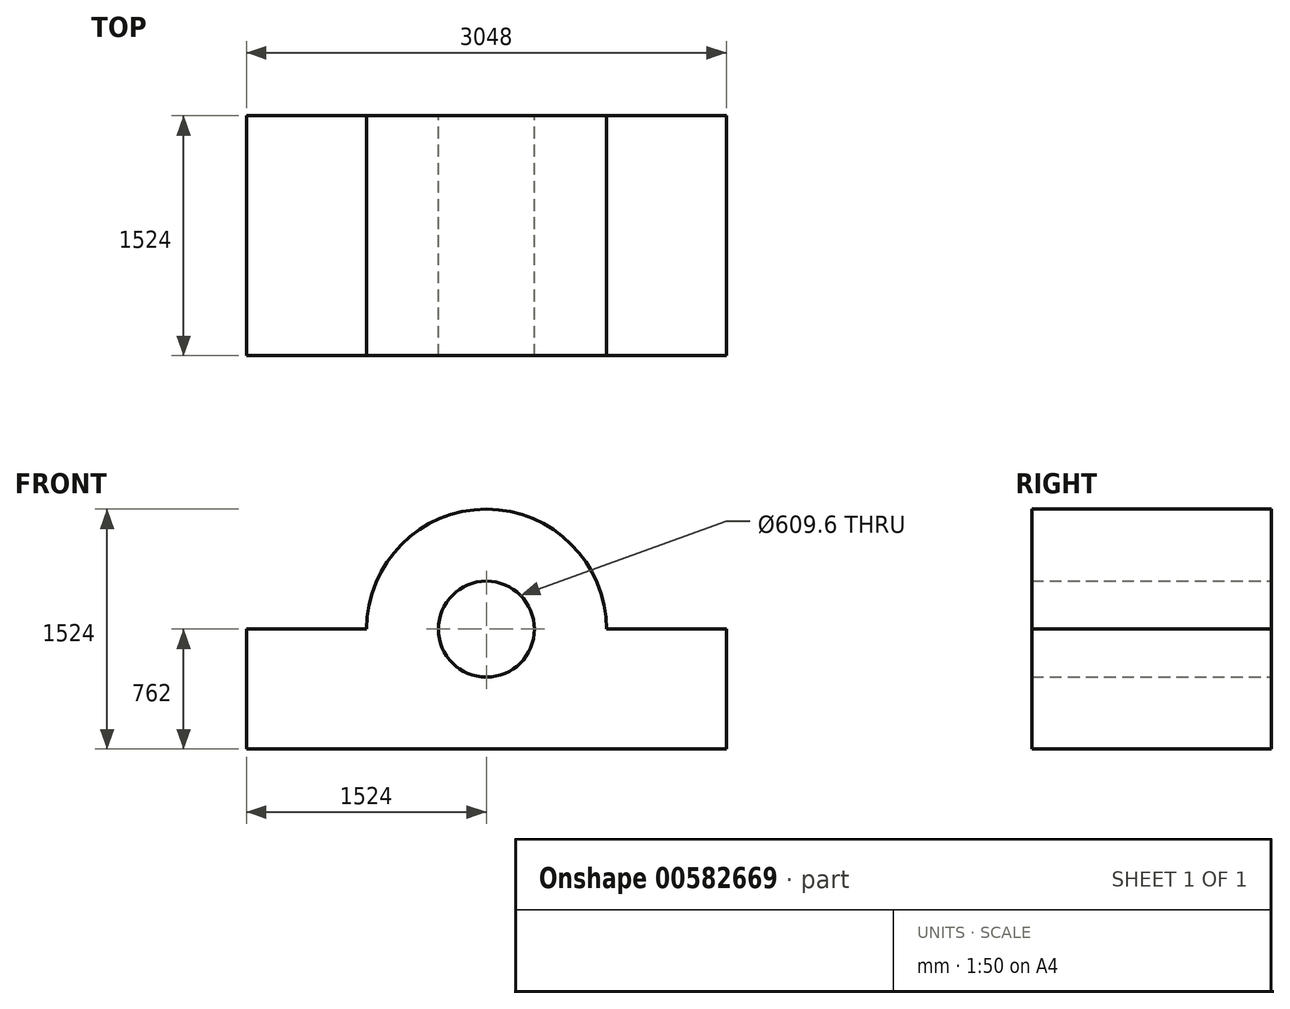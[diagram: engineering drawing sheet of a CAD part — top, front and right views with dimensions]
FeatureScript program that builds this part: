
annotation { "Feature Type Name" : "Feature", "Feature Type Description" : "" }
export const myFeature = defineFeature(function(context is Context, id is Id, definition is map)
    precondition{}
    {
        {
            var Q0;
            Q0=qCreatedBy(makeId("Front.planeOp"),FACE);
            var sketch = newSketch(context, id + "F0", { "sketchPlane" : qUnion([Q0])});
            skLineSegment(sketch, "E0", {"start": v(0, 0) * mm, "end": v(3048, 0) * mm});
            skLineSegment(sketch, "E1", {"start": v(3048, 0) * mm, "end": v(3048, 762) * mm});
            skLineSegment(sketch, "E2", {"start": v(3048, 762) * mm, "end": v(2286, 762) * mm});
            skLineSegment(sketch, "E3", {"start": v(0, 0) * mm, "end": v(0, 762) * mm});
            skLineSegment(sketch, "E4", {"start": v(0, 762) * mm, "end": v(762, 762) * mm});
            skArc(sketch, "E5", {"start": v(2286, 762) * mm, "mid": v(1524, 1524) * mm, "end": v(762, 762) * mm});
            skPoint(sketch, "E5.centerSnap0", {"position": v(1524, 0) * mm});
            skCircle(sketch, "E6", {"center": v(1524, 762) * mm, "radius": 304.8 * mm});
            skSolve(sketch);
        }
        {
            var Q0;
            Q0=makeQuery(id+"F0.imprint","IMPRINT",FACE,{"disambiguationData":[TD([[makeQuery(id+"F0.imprint","IMPRINT",EDGE,{"derivedFrom":sQuery(id+"F0.wireOp",EDGE,"E0")}),1.0]])]});
            extrude(context, id + "F1", {"entities" : qUnion([Q0]), "depth" : 1524 * mm, "offsetDistance" : 25.4 * mm});
        }
    });
